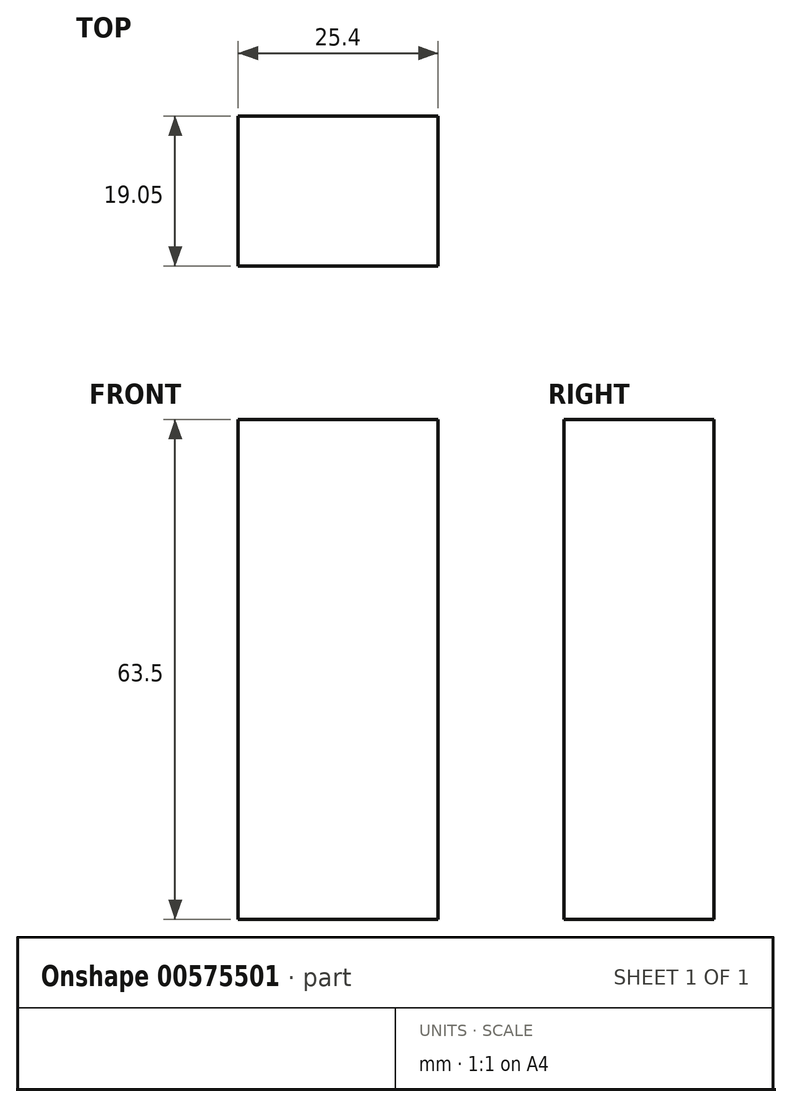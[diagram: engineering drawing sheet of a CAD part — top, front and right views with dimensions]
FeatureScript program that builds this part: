
annotation { "Feature Type Name" : "Feature", "Feature Type Description" : "" }
export const myFeature = defineFeature(function(context is Context, id is Id, definition is map)
    precondition{}
    {
        {
            var Q0;
            Q0=qCreatedBy(makeId("Front.planeOp"),FACE);
            var sketch = newSketch(context, id + "F0", { "sketchPlane" : qUnion([Q0])});
            skLineSegment(sketch, "E0.bottom", {"start": v(-72.75, 123.42) * mm, "end": v(-34.65, 123.42) * mm});
            skLineSegment(sketch, "E0.top", {"start": v(-72.75, -130.58) * mm, "end": v(-34.65, -130.58) * mm});
            skLineSegment(sketch, "E0.left", {"start": v(-72.75, 123.42) * mm, "end": v(-72.75, -130.58) * mm});
            skLineSegment(sketch, "E1.bottom", {"start": v(-53.7, 123.42) * mm, "end": v(43.18, 123.42) * mm});
            skLineSegment(sketch, "E1.top", {"start": v(-53.7, -131.36) * mm, "end": v(43.18, -131.36) * mm});
            skLineSegment(sketch, "E1.right", {"start": v(43.18, 123.42) * mm, "end": v(43.18, -131.36) * mm});
            skLineSegment(sketch, "E2.bottom", {"start": v(-5.26, 123.42) * mm, "end": v(20.14, 123.42) * mm});
            skLineSegment(sketch, "E2.top", {"start": v(-5.26, 186.92) * mm, "end": v(20.14, 186.92) * mm});
            skLineSegment(sketch, "E2.left", {"start": v(-5.26, 123.42) * mm, "end": v(-5.26, 186.92) * mm});
            skLineSegment(sketch, "E2.right", {"start": v(20.14, 123.42) * mm, "end": v(20.14, 186.92) * mm});
            skLineSegment(sketch, "E3.bottom", {"start": v(43.18, 123.42) * mm, "end": v(-72.75, 123.42) * mm});
            skLineSegment(sketch, "E3.top", {"start": v(43.18, -130.58) * mm, "end": v(-72.75, -130.58) * mm});
            skLineSegment(sketch, "E3.left", {"start": v(43.18, 123.42) * mm, "end": v(43.18, -130.58) * mm});
            skSolve(sketch);
        }
        {
            var Q0;
            {var subQ0=sQuery(id+"F0.wireOp",EDGE,"E3.left");Q0=makeQuery(id+"F0.imprint","IMPRINT",FACE,{"disambiguationData":[TD([[makeQuery(id+"F0.imprint","IMPRINT",EDGE,{"derivedFrom":subQ0}),-1.0]])]});}
            var Q1;
            Q1=makeQuery(id+"F0.imprint","IMPRINT",FACE,{"disambiguationData":[TD([[makeQuery(id+"F0.imprint","IMPRINT",EDGE,{"derivedFrom":sQuery(id+"F0.wireOp",EDGE,"E2.top")}),-1.0]])]});
            extrude(context, id + "F1", {"entities" : qUnion([Q0, Q1]), "depth" : 19.05 * mm, "offsetDistance" : 25.4 * mm});
        }
    });
